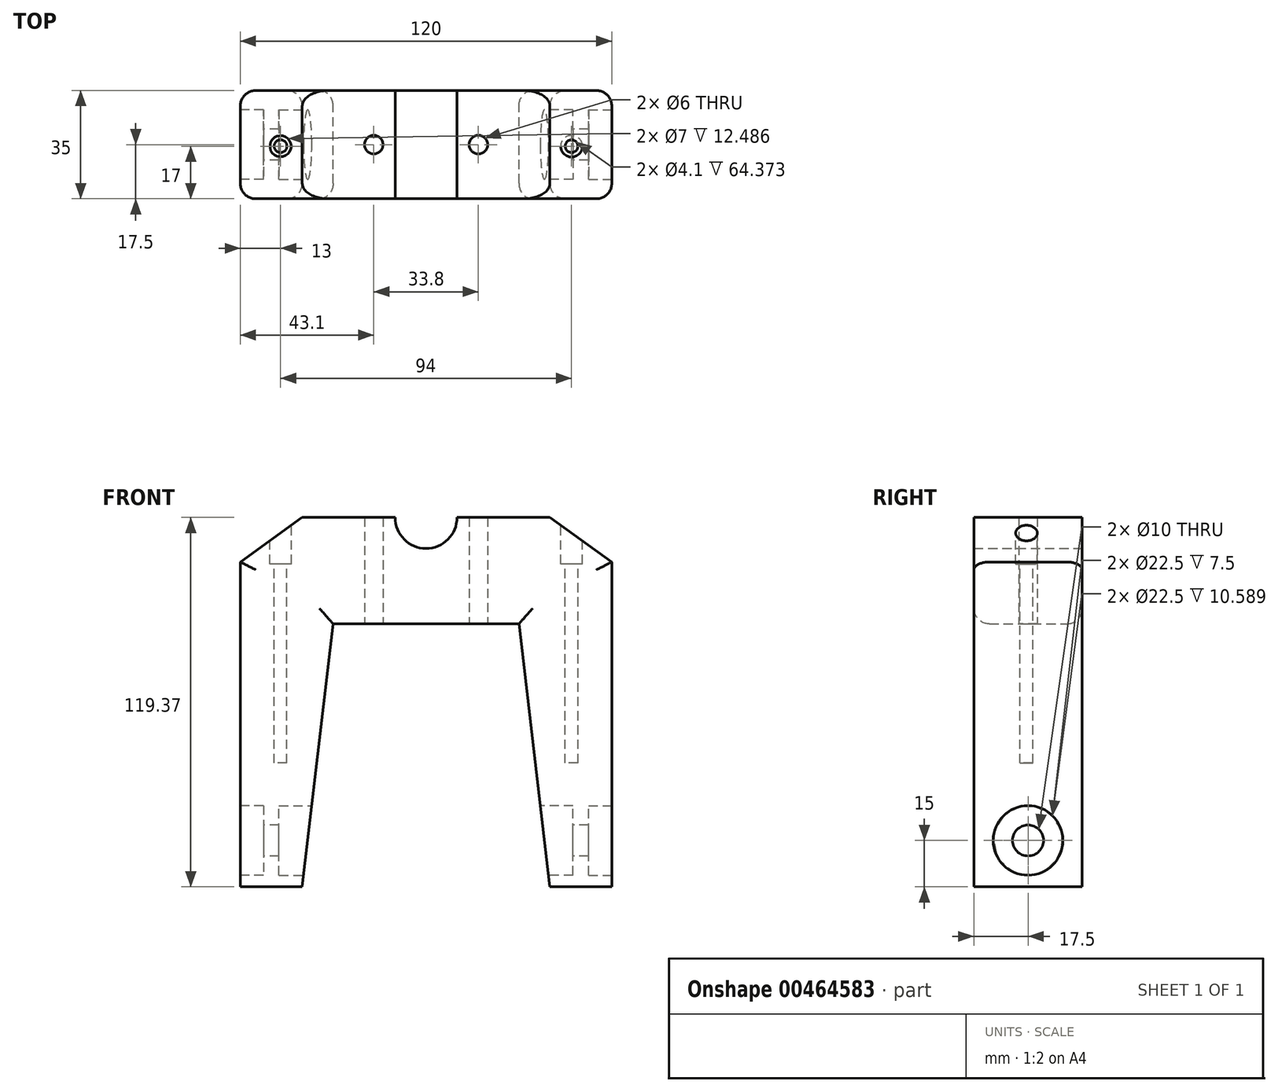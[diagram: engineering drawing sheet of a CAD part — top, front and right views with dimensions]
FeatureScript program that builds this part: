
annotation { "Feature Type Name" : "Feature", "Feature Type Description" : "" }
export const myFeature = defineFeature(function(context is Context, id is Id, definition is map)
    precondition{}
    {
        {
            var Q0;
            Q0=qCreatedBy(makeId("Front.planeOp"),FACE);
            var sketch = newSketch(context, id + "F0", { "sketchPlane" : qUnion([Q0])});
            skLineSegment(sketch, "E0", {"start": v(0, 0) * mm, "end": v(60, 0) * mm, "construction": true});
            skLineSegment(sketch, "E1", {"start": v(0, 0) * mm, "end": v(0, 19.37) * mm, "construction": true});
            skLineSegment(sketch, "E2", {"start": v(0, 0) * mm, "end": v(-60, 0) * mm, "construction": true});
            skLineSegment(sketch, "E3", {"start": v(0, 0) * mm, "end": v(0, -15) * mm, "construction": true});
            skLineSegment(sketch, "E4", {"start": v(-60, 5) * mm, "end": v(-60, 0) * mm});
            skLineSegment(sketch, "E5", {"start": v(-60, 0) * mm, "end": v(-60, -100) * mm});
            skLineSegment(sketch, "E6", {"start": v(60, 0) * mm, "end": v(60, -100) * mm});
            skLineSegment(sketch, "E7", {"start": v(60, 0) * mm, "end": v(60, 5) * mm});
            skArc(sketch, "E8", {"start": v(-10, 19.37) * mm, "mid": v(0, 9.37) * mm, "end": v(10, 19.37) * mm});
            skLineSegment(sketch, "E9", {"start": v(-60, -100) * mm, "end": v(-40, -100) * mm});
            skLineSegment(sketch, "E10", {"start": v(60, -100) * mm, "end": v(40, -100) * mm});
            skLineSegment(sketch, "E11", {"start": v(0, -15) * mm, "end": v(-30, -15) * mm});
            skLineSegment(sketch, "E12", {"start": v(0, -15) * mm, "end": v(30, -15) * mm});
            skLineSegment(sketch, "E13", {"start": v(-40, -100) * mm, "end": v(-30, -15) * mm});
            skLineSegment(sketch, "E14", {"start": v(30, -15) * mm, "end": v(40, -100) * mm});
            skLineSegment(sketch, "E15", {"start": v(-10, 19.37) * mm, "end": v(-40, 19.37) * mm});
            skLineSegment(sketch, "E16", {"start": v(-40, 19.37) * mm, "end": v(-60, 5) * mm});
            skLineSegment(sketch, "E17", {"start": v(10, 19.37) * mm, "end": v(40, 19.37) * mm});
            skLineSegment(sketch, "E18", {"start": v(40, 19.37) * mm, "end": v(60, 5) * mm});
            skSolve(sketch);
        }
        {
            var Q0;
            Q0=qSketchRegion(id+"F0",true);
            extrude(context, id + "F1", {"entities" : qUnion([Q0]), "depth" : 35 * mm, "offsetDistance" : 25 * mm});
        }
        {
            var Q0;
            Q0=makeQuery(id+"F1.opExtrude","SWEPT_FACE",FACE,{"disambiguationData":[OSD([sQuery(id+"F0.wireOp",EDGE,"E11"),sQuery(id+"F0.wireOp",EDGE,"E12")])]});
            var sketch = newSketch(context, id + "F2", { "sketchPlane" : qUnion([Q0])});
            skCircle(sketch, "E19", {"center": v(-16.9, 17.5) * mm, "radius": 3 * mm});
            skLineSegment(sketch, "E20", {"start": v(-16.9, 17.5) * mm, "end": v(16.9, 17.5) * mm, "construction": true});
            skCircle(sketch, "E21", {"center": v(16.9, 17.5) * mm, "radius": 3 * mm});
            skSolve(sketch);
        }
        {
            var Q0;
            Q0=qSketchRegion(id+"F2",true);
            extrude(context, id + "F3", {"entities" : qUnion([Q0]), "operationType" : NewBodyOperationType.REMOVE, "endBound" : BoundingType.THROUGH_ALL, "oppositeDirection" : true, "depth" : 25 * mm, "offsetDistance" : 25 * mm});
        }
        {
            var Q0;
            Q0=makeQuery(id+"F1.opExtrude","SWEPT_FACE",FACE,{"disambiguationData":[OSD([sQuery(id+"F0.wireOp",EDGE,"E4"),sQuery(id+"F0.wireOp",EDGE,"E5")])]});
            var sketch = newSketch(context, id + "F4", { "sketchPlane" : qUnion([Q0])});
            skCircle(sketch, "E22", {"center": v(17.5, -85) * mm, "radius": 5 * mm});
            skSolve(sketch);
        }
        {
            var Q0;
            Q0=qSketchRegion(id+"F4",true);
            extrude(context, id + "F5", {"entities" : qUnion([Q0]), "operationType" : NewBodyOperationType.REMOVE, "endBound" : BoundingType.THROUGH_ALL, "oppositeDirection" : true, "depth" : 25 * mm, "offsetDistance" : 25 * mm});
        }
        {
            var Q0;
            Q0=makeQuery(id+"F1.opExtrude","SWEPT_FACE",FACE,{"disambiguationData":[OSD([sQuery(id+"F0.wireOp",EDGE,"E4"),sQuery(id+"F0.wireOp",EDGE,"E5")])]});
            var sketch = newSketch(context, id + "F6", { "sketchPlane" : qUnion([Q0])});
            skCircle(sketch, "E23", {"center": v(17.5, -85) * mm, "radius": 11.25 * mm});
            skSolve(sketch);
        }
        {
            var Q0;
            Q0=qSketchRegion(id+"F6",true);
            extrude(context, id + "F7", {"entities" : qUnion([Q0]), "operationType" : NewBodyOperationType.REMOVE, "oppositeDirection" : true, "depth" : 7.5 * mm, "offsetDistance" : 25 * mm});
        }
        {
            var Q0;
            Q0=makeQuery(id+"F1.opExtrude","SWEPT_FACE",FACE,{"disambiguationData":[OSD([sQuery(id+"F0.wireOp",EDGE,"E6"),sQuery(id+"F0.wireOp",EDGE,"E7")])]});
            var sketch = newSketch(context, id + "F8", { "sketchPlane" : qUnion([Q0])});
            skCircle(sketch, "E24", {"center": v(-17.5, -85) * mm, "radius": 11.25 * mm});
            skSolve(sketch);
        }
        {
            var Q0;
            Q0=qSketchRegion(id+"F8",true);
            extrude(context, id + "F9", {"entities" : qUnion([Q0]), "operationType" : NewBodyOperationType.REMOVE, "oppositeDirection" : true, "depth" : 7.5 * mm, "offsetDistance" : 25 * mm});
        }
        {
            var Q0;
            Q0=qCreatedBy(makeId("Right.planeOp"),FACE);
            var sketch = newSketch(context, id + "F10", { "sketchPlane" : qUnion([Q0])});
            skCircle(sketch, "E25", {"center": v(-17.5, -85) * mm, "radius": 11.25 * mm});
            skSolve(sketch);
        }
        {
            var Q0;
            Q0=qSketchRegion(id+"F10",true);
            extrude(context, id + "F11", {"entities" : qUnion([Q0]), "operationType" : NewBodyOperationType.REMOVE, "oppositeDirection" : true, "depth" : 47.5 * mm, "offsetDistance" : 25 * mm});
        }
        {
            var Q0;
            Q0=qCreatedBy(makeId("Right.planeOp"),FACE);
            var sketch = newSketch(context, id + "F12", { "sketchPlane" : qUnion([Q0])});
            skCircle(sketch, "E26", {"center": v(-17.5, -85) * mm, "radius": 11.25 * mm});
            skSolve(sketch);
        }
        {
            var Q0;
            Q0=qSketchRegion(id+"F12",true);
            extrude(context, id + "F13", {"entities" : qUnion([Q0]), "operationType" : NewBodyOperationType.REMOVE, "depth" : 47.5 * mm, "offsetDistance" : 25 * mm});
        }
        {
            var Q0;
            Q0=qCreatedBy(makeId("Top.planeOp"),FACE);
            var sketch = newSketch(context, id + "F14", { "sketchPlane" : qUnion([Q0])});
            skCircle(sketch, "E27", {"center": v(-47, -18) * mm, "radius": 2.05 * mm});
            skCircle(sketch, "E28", {"center": v(47, -18) * mm, "radius": 2.05 * mm});
            skSolve(sketch);
        }
        {
            var Q0;
            Q0 = qSketchRegion(id + "F14", true);
            extrude(context, id + "F15", {"entities" : qUnion([Q0]), "operationType" : NewBodyOperationType.REMOVE, "endBound" : BoundingType.SYMMETRIC, "oppositeDirection" : true, "depth" : 120 * mm, "offsetDistance" : 25 * mm});
        }
        {
            var Q0;
            Q0=makeQuery(id+"F1.opExtrude","SWEPT_FACE",FACE,{"disambiguationData":[OSD([sQuery(id+"F0.wireOp",EDGE,"E15")])]});
            var sketch = newSketch(context, id + "F16", { "sketchPlane" : qUnion([Q0])});
            skCircle(sketch, "E29", {"center": v(-47, -18) * mm, "radius": 3.5 * mm});
            skCircle(sketch, "E30", {"center": v(47, -18) * mm, "radius": 3.5 * mm});
            skSolve(sketch);
        }
        {
            var Q0;
            Q0 = qSketchRegion(id + "F16", true);
            extrude(context, id + "F17", {"entities" : qUnion([Q0]), "operationType" : NewBodyOperationType.REMOVE, "oppositeDirection" : true, "depth" : 15 * mm, "offsetDistance" : 25 * mm});
        }
        {
            var Q0;
            Q0=makeQuery(id+"F1.opExtrude","CAP_EDGE",EDGE,{"disambiguationData":[OSD([sQuery(id+"F0.wireOp",EDGE,"E6"),sQuery(id+"F0.wireOp",EDGE,"E7")])],"isStart":false});
            var Q1;
            Q1=makeQuery(id+"F1.opExtrude","CAP_EDGE",EDGE,{"disambiguationData":[OSD([sQuery(id+"F0.wireOp",EDGE,"E6"),sQuery(id+"F0.wireOp",EDGE,"E7")])],"isStart":true});
            var Q2;
            Q2=makeQuery(id+"F1.opExtrude","CAP_EDGE",EDGE,{"disambiguationData":[OSD([sQuery(id+"F0.wireOp",EDGE,"E4"),sQuery(id+"F0.wireOp",EDGE,"E5")])],"isStart":false});
            var Q3;
            Q3=makeQuery(id+"F1.opExtrude","CAP_EDGE",EDGE,{"disambiguationData":[OSD([sQuery(id+"F0.wireOp",EDGE,"E4"),sQuery(id+"F0.wireOp",EDGE,"E5")])],"isStart":true});
            var Q4;
            Q4=makeQuery(id+"F1.opExtrude","CAP_EDGE",EDGE,{"disambiguationData":[OSD([sQuery(id+"F0.wireOp",EDGE,"E16")])],"isStart":true});
            var Q5;
            Q5=makeQuery(id+"F1.opExtrude","CAP_EDGE",EDGE,{"disambiguationData":[OSD([sQuery(id+"F0.wireOp",EDGE,"E16")])],"isStart":false});
            var Q6;
            Q6=makeQuery(id+"F1.opExtrude","CAP_EDGE",EDGE,{"disambiguationData":[OSD([sQuery(id+"F0.wireOp",EDGE,"E18")])],"isStart":false});
            var Q7;
            Q7=makeQuery(id+"F1.opExtrude","CAP_EDGE",EDGE,{"disambiguationData":[OSD([sQuery(id+"F0.wireOp",EDGE,"E18")])],"isStart":true});
            var Q8;
            Q8=makeQuery(id+"F1.opExtrude","CAP_EDGE",EDGE,{"disambiguationData":[OSD([sQuery(id+"F0.wireOp",EDGE,"E14")])],"isStart":true});
            var Q9;
            Q9=makeQuery(id+"F1.opExtrude","CAP_EDGE",EDGE,{"disambiguationData":[OSD([sQuery(id+"F0.wireOp",EDGE,"E11"),sQuery(id+"F0.wireOp",EDGE,"E12")])],"isStart":true});
            var Q10;
            Q10=makeQuery(id+"F1.opExtrude","CAP_EDGE",EDGE,{"disambiguationData":[OSD([sQuery(id+"F0.wireOp",EDGE,"E11"),sQuery(id+"F0.wireOp",EDGE,"E12")])],"isStart":false});
            var Q11;
            Q11=makeQuery(id+"F1.opExtrude","CAP_EDGE",EDGE,{"disambiguationData":[OSD([sQuery(id+"F0.wireOp",EDGE,"E13")])],"isStart":false});
            var Q12;
            Q12=makeQuery(id+"F1.opExtrude","CAP_EDGE",EDGE,{"disambiguationData":[OSD([sQuery(id+"F0.wireOp",EDGE,"E14")])],"isStart":false});
            var Q13;
            Q13=makeQuery(id+"F1.opExtrude","CAP_EDGE",EDGE,{"disambiguationData":[OSD([sQuery(id+"F0.wireOp",EDGE,"E13")])],"isStart":true});
            fillet(context, id + "F18", {"entities" : qUnion([Q0, Q1, Q2, Q3, Q4, Q5, Q6, Q7, Q8, Q9, Q10, Q11, Q12, Q13]), "radius" : 5 * mm, "tangentPropagation" : true, "allowEdgeOverflow" : false});
        }
    });
